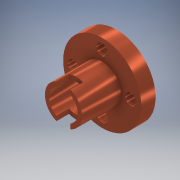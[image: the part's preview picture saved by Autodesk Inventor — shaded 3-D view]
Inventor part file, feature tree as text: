
AUTODESK INVENTOR PART (.ipt)
format: ipt  version: 2017 SP1 (Build 210196100, 196)  size: 154,112 bytes
history: native  units: mm
features: sketch x4, extrude x3, other x1, hole x1, projected_geometry x1
ambient origin geometry x8: Origin, YZ Plane, XZ Plane, XY Plane, X Axis, Y Axis, Z Axis, Center Point
bodies: Body1 (feature_tree)
feature tree (10):
  other  "Bryła1"
  extrude  "Wyciągnięcie proste1"  Depth=21.75mm
  hole  "Otwór1"  [1 undecoded]
  extrude  "Wyciągnięcie proste2"  Depth=8.0mm
  extrude  "Wyciągnięcie proste3"  Depth=40.0mm TaperAngle=360.0deg
  sketch  "Szkic1"
  sketch  "Szkic2"
  projected_geometry  "Pętla rzutowana1"
  sketch  "Szkic3"
  sketch  "Szkic4"
note: 1 required parameter value undecoded (feature->parameter linkage not recoverable at this tier; creation-order binding heuristic only, values carry confidence <= 0.55)
